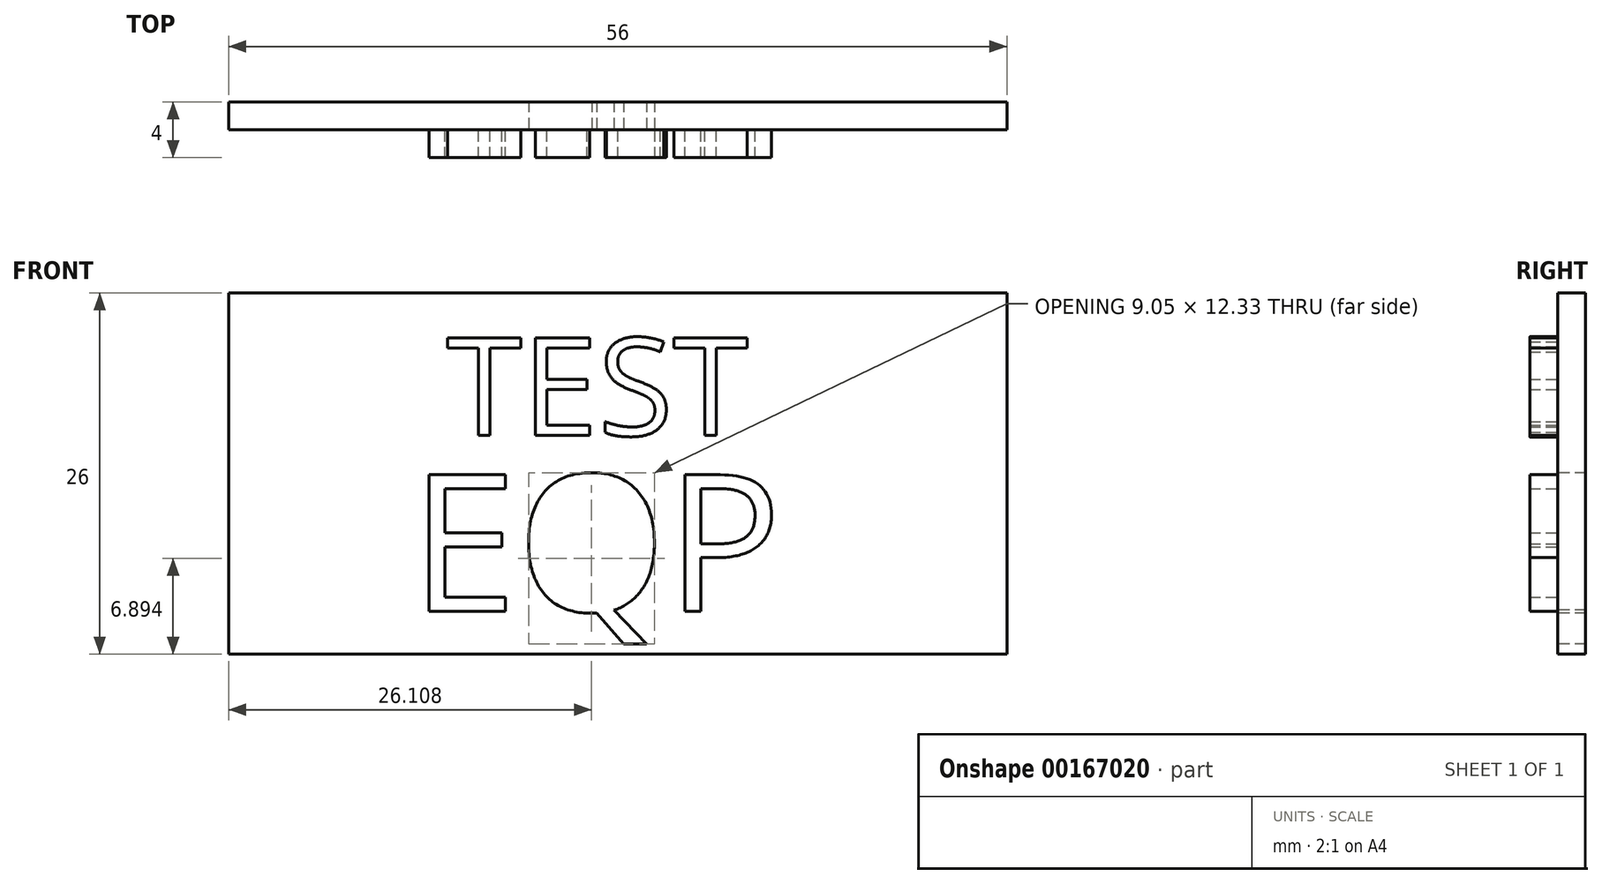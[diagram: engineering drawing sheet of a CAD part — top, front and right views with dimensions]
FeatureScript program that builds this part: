
annotation { "Feature Type Name" : "Feature", "Feature Type Description" : "" }
export const myFeature = defineFeature(function(context is Context, id is Id, definition is map)
    precondition{}
    {
        {
            var Q0;
            Q0=qCreatedBy(makeId("Front.planeOp"),FACE);
            var sketch = newSketch(context, id + "F0", { "sketchPlane" : qUnion([Q0])});
            skLineSegment(sketch, "E0", {"start": v(0, 0) * mm, "end": v(-56, 0) * mm});
            skLineSegment(sketch, "E1", {"start": v(-56, 0) * mm, "end": v(-56, 26) * mm});
            skLineSegment(sketch, "E2", {"start": v(-56, 26) * mm, "end": v(0, 26) * mm});
            skLineSegment(sketch, "E3", {"start": v(0, 26) * mm, "end": v(0, 0) * mm});
            skText(sketch, "E4", { "text": "EQP", "fontName": "OpenSans-Regular.ttf"});
            skText(sketch, "E5", { "text": "TEST", "fontName": "OpenSans-Regular.ttf"});
            const initialGuessF0  = {"E4": [-0.04292, 0.00307, 1, 0, 0.00992], "E5": [-0.04034, 0.01573, 1, 0, 0.00708]};
            skSetInitialGuess(sketch, initialGuessF0);
            skSolve(sketch);
        }
        {
            var Q0;
            Q0=qSketchRegion(id+"F0",true);
            var Q1;
            Q1=makeQuery(id+"F0.imprint","IMPRINT",FACE,{"disambiguationData":[TD([[makeQuery(id+"F0.imprint","IMPRINT",EDGE,{"derivedFrom":sQuery(id+"F0.wireOp",EDGE,"85295631-b2a8-45b6-9694-f0444079e252.sketch_text.stroke-0")}),-1.0]])]});
            var Q2;
            Q2=makeQuery(id+"F0.imprint","IMPRINT",FACE,{"disambiguationData":[TD([[makeQuery(id+"F0.imprint","IMPRINT",EDGE,{"derivedFrom":sQuery(id+"F0.wireOp",EDGE,"85295631-b2a8-45b6-9694-f0444079e252.sketch_text.stroke-7")}),1.0]])]});
            var Q3;
            Q3=makeQuery(id+"F0.imprint","IMPRINT",FACE,{"disambiguationData":[TD([[makeQuery(id+"F0.imprint","IMPRINT",EDGE,{"derivedFrom":sQuery(id+"F0.wireOp",EDGE,"85295631-b2a8-45b6-9694-f0444079e252.sketch_text.stroke-14")}),-1.0]])]});
            var Q4;
            Q4=makeQuery(id+"F0.imprint","IMPRINT",FACE,{"disambiguationData":[TD([[makeQuery(id+"F0.imprint","IMPRINT",EDGE,{"derivedFrom":sQuery(id+"F0.wireOp",EDGE,"E4.sketch_text.stroke-0")}),-1.0]])]});
            var Q5;
            Q5=makeQuery(id+"F0.imprint","IMPRINT",FACE,{"disambiguationData":[TD([[makeQuery(id+"F0.imprint","IMPRINT",EDGE,{"derivedFrom":sQuery(id+"F0.wireOp",EDGE,"E4.sketch_text.stroke-8")}),1.0]])]});
            var Q6;
            Q6=makeQuery(id+"F0.imprint","IMPRINT",FACE,{"disambiguationData":[TD([[makeQuery(id+"F0.imprint","IMPRINT",EDGE,{"derivedFrom":sQuery(id+"F0.wireOp",EDGE,"E4.sketch_text.stroke-16")}),-1.0]])]});
            var Q7;
            Q7=makeQuery(id+"F0.imprint","IMPRINT",FACE,{"disambiguationData":[TD([[makeQuery(id+"F0.imprint","IMPRINT",EDGE,{"derivedFrom":sQuery(id+"F0.wireOp",EDGE,"85295631-b2a8-45b6-9694-f0444079e252.sketch_text.stroke-26")}),-1.0]])]});
            var Q8;
            Q8=makeQuery(id+"F0.imprint","IMPRINT",FACE,{"disambiguationData":[TD([[makeQuery(id+"F0.imprint","IMPRINT",EDGE,{"derivedFrom":sQuery(id+"F0.wireOp",EDGE,"85295631-b2a8-45b6-9694-f0444079e252.sketch_text.stroke-54")}),-1.0]])]});
            var Q9;
            Q9=makeQuery(id+"F0.imprint","IMPRINT",FACE,{"disambiguationData":[TD([[makeQuery(id+"F0.imprint","IMPRINT",EDGE,{"derivedFrom":sQuery(id+"F0.wireOp",EDGE,"85295631-b2a8-45b6-9694-f0444079e252.sketch_text.stroke-66")}),-1.0]])]});
            var Q10;
            Q10=makeQuery(id+"F0.imprint","IMPRINT",FACE,{"disambiguationData":[TD([[makeQuery(id+"F0.imprint","IMPRINT",EDGE,{"derivedFrom":sQuery(id+"F0.wireOp",EDGE,"85295631-b2a8-45b6-9694-f0444079e252.sketch_text.stroke-58")}),-1.0]])]});
            var Q11;
            Q11=makeQuery(id+"F0.imprint","IMPRINT",FACE,{"disambiguationData":[TD([[makeQuery(id+"F0.imprint","IMPRINT",EDGE,{"derivedFrom":sQuery(id+"F0.wireOp",EDGE,"E4.sketch_text.stroke-27")}),1.0]])]});
            var Q12;
            Q12=makeQuery(id+"F0.imprint","IMPRINT",FACE,{"disambiguationData":[TD([[makeQuery(id+"F0.imprint","IMPRINT",EDGE,{"derivedFrom":sQuery(id+"F0.wireOp",EDGE,"E4.sketch_text.stroke-32")}),-1.0]])]});
            var Q13;
            Q13=makeQuery(id+"F0.imprint","IMPRINT",FACE,{"disambiguationData":[TD([[makeQuery(id+"F0.imprint","IMPRINT",EDGE,{"derivedFrom":sQuery(id+"F0.wireOp",EDGE,"E4.sketch_text.stroke-40")}),1.0]])]});
            var Q14;
            Q14=makeQuery(id+"F0.imprint","IMPRINT",FACE,{"disambiguationData":[TD([[makeQuery(id+"F0.imprint","IMPRINT",EDGE,{"derivedFrom":sQuery(id+"F0.wireOp",EDGE,"E5.sketch_text.stroke-45")}),-1.0]])]});
            var Q15;
            Q15=makeQuery(id+"F0.imprint","IMPRINT",FACE,{"disambiguationData":[TD([[makeQuery(id+"F0.imprint","IMPRINT",EDGE,{"derivedFrom":sQuery(id+"F0.wireOp",EDGE,"E5.sketch_text.stroke-20")}),-1.0]])]});
            var Q16;
            Q16=makeQuery(id+"F0.imprint","IMPRINT",FACE,{"disambiguationData":[TD([[makeQuery(id+"F0.imprint","IMPRINT",EDGE,{"derivedFrom":sQuery(id+"F0.wireOp",EDGE,"E5.sketch_text.stroke-8")}),-1.0]])]});
            var Q17;
            Q17=makeQuery(id+"F0.imprint","IMPRINT",FACE,{"disambiguationData":[TD([[makeQuery(id+"F0.imprint","IMPRINT",EDGE,{"derivedFrom":sQuery(id+"F0.wireOp",EDGE,"E5.sketch_text.stroke-0")}),-1.0]])]});
            extrude(context, id + "F1", {"entities" : qUnion([Q0, Q1, Q2, Q3, Q4, Q5, Q6, Q7, Q8, Q9, Q10, Q11, Q12, Q13, Q14, Q15, Q16, Q17]), "oppositeDirection" : true, "depth" : 2 * mm, "offsetDistance" : 25 * mm});
        }
        {
            var Q0;
            Q0=makeQuery(id+"F0.imprint","IMPRINT",FACE,{"disambiguationData":[TD([[makeQuery(id+"F0.imprint","IMPRINT",EDGE,{"derivedFrom":sQuery(id+"F0.wireOp",EDGE,"85295631-b2a8-45b6-9694-f0444079e252.sketch_text.stroke-66")}),-1.0]])]});
            var Q1;
            Q1=makeQuery(id+"F0.imprint","IMPRINT",FACE,{"disambiguationData":[TD([[makeQuery(id+"F0.imprint","IMPRINT",EDGE,{"derivedFrom":sQuery(id+"F0.wireOp",EDGE,"85295631-b2a8-45b6-9694-f0444079e252.sketch_text.stroke-54")}),-1.0]])]});
            var Q2;
            Q2=makeQuery(id+"F0.imprint","IMPRINT",FACE,{"disambiguationData":[TD([[makeQuery(id+"F0.imprint","IMPRINT",EDGE,{"derivedFrom":sQuery(id+"F0.wireOp",EDGE,"85295631-b2a8-45b6-9694-f0444079e252.sketch_text.stroke-58")}),-1.0]])]});
            var Q3;
            Q3=makeQuery(id+"F0.imprint","IMPRINT",FACE,{"disambiguationData":[TD([[makeQuery(id+"F0.imprint","IMPRINT",EDGE,{"derivedFrom":sQuery(id+"F0.wireOp",EDGE,"85295631-b2a8-45b6-9694-f0444079e252.sketch_text.stroke-26")}),-1.0]])]});
            var Q4;
            Q4=makeQuery(id+"F0.imprint","IMPRINT",FACE,{"disambiguationData":[TD([[makeQuery(id+"F0.imprint","IMPRINT",EDGE,{"derivedFrom":sQuery(id+"F0.wireOp",EDGE,"85295631-b2a8-45b6-9694-f0444079e252.sketch_text.stroke-14")}),-1.0]])]});
            var Q5;
            Q5=makeQuery(id+"F0.imprint","IMPRINT",FACE,{"disambiguationData":[TD([[makeQuery(id+"F0.imprint","IMPRINT",EDGE,{"derivedFrom":sQuery(id+"F0.wireOp",EDGE,"85295631-b2a8-45b6-9694-f0444079e252.sketch_text.stroke-0")}),-1.0]])]});
            var Q6;
            Q6=makeQuery(id+"F0.imprint","IMPRINT",FACE,{"disambiguationData":[TD([[makeQuery(id+"F0.imprint","IMPRINT",EDGE,{"derivedFrom":sQuery(id+"F0.wireOp",EDGE,"E4.sketch_text.stroke-0")}),-1.0]])]});
            var Q7;
            Q7=makeQuery(id+"F0.imprint","IMPRINT",FACE,{"disambiguationData":[TD([[makeQuery(id+"F0.imprint","IMPRINT",EDGE,{"derivedFrom":sQuery(id+"F0.wireOp",EDGE,"E4.sketch_text.stroke-16")}),-1.0]])]});
            var Q8;
            Q8=makeQuery(id+"F0.imprint","IMPRINT",FACE,{"disambiguationData":[TD([[makeQuery(id+"F0.imprint","IMPRINT",EDGE,{"derivedFrom":sQuery(id+"F0.wireOp",EDGE,"E4.sketch_text.stroke-32")}),-1.0]])]});
            var Q9;
            Q9=makeQuery(id+"F0.imprint","IMPRINT",FACE,{"disambiguationData":[TD([[makeQuery(id+"F0.imprint","IMPRINT",EDGE,{"derivedFrom":sQuery(id+"F0.wireOp",EDGE,"E5.sketch_text.stroke-45")}),-1.0]])]});
            var Q10;
            Q10=makeQuery(id+"F0.imprint","IMPRINT",FACE,{"disambiguationData":[TD([[makeQuery(id+"F0.imprint","IMPRINT",EDGE,{"derivedFrom":sQuery(id+"F0.wireOp",EDGE,"E5.sketch_text.stroke-20")}),-1.0]])]});
            var Q11;
            Q11=makeQuery(id+"F0.imprint","IMPRINT",FACE,{"disambiguationData":[TD([[makeQuery(id+"F0.imprint","IMPRINT",EDGE,{"derivedFrom":sQuery(id+"F0.wireOp",EDGE,"E5.sketch_text.stroke-8")}),-1.0]])]});
            var Q12;
            Q12=makeQuery(id+"F0.imprint","IMPRINT",FACE,{"disambiguationData":[TD([[makeQuery(id+"F0.imprint","IMPRINT",EDGE,{"derivedFrom":sQuery(id+"F0.wireOp",EDGE,"E5.sketch_text.stroke-0")}),-1.0]])]});
            extrude(context, id + "F2", {"entities" : qUnion([Q0, Q1, Q2, Q3, Q4, Q5, Q6, Q7, Q8, Q9, Q10, Q11, Q12]), "operationType" : NewBodyOperationType.ADD, "depth" : 2 * mm, "offsetDistance" : 25 * mm});
        }
    });
